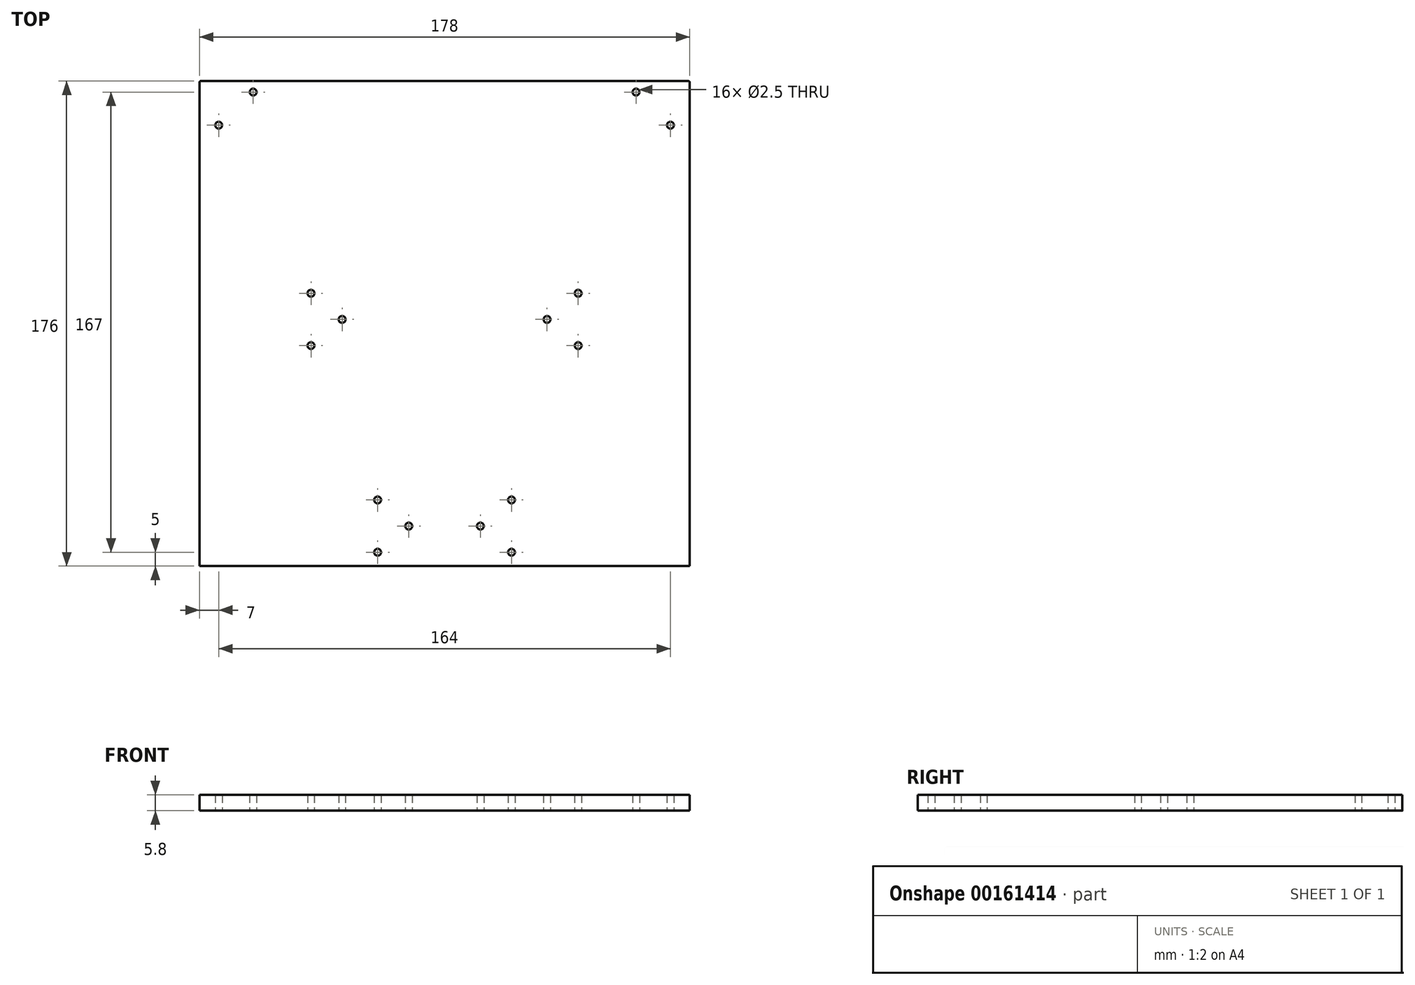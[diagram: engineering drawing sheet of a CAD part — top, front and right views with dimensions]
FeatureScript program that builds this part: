
annotation { "Feature Type Name" : "Feature", "Feature Type Description" : "" }
export const myFeature = defineFeature(function(context is Context, id is Id, definition is map)
    precondition{}
    {
        {
            var Q0;
            Q0=qCreatedBy(makeId("Top.planeOp"),FACE);
            var sketch = newSketch(context, id + "F0", { "sketchPlane" : qUnion([Q0])});
            skLineSegment(sketch, "E0.bottom", {"start": v(88.5, 88) * mm, "end": v(-88.5, 88) * mm});
            skLineSegment(sketch, "E0.top", {"start": v(89, -88) * mm, "end": v(58.5, -88) * mm});
            skLineSegment(sketch, "E0.left", {"start": v(89, 87.5) * mm, "end": v(89, -88) * mm});
            skLineSegment(sketch, "E0.right", {"start": v(-89, 87.5) * mm, "end": v(-89, -88) * mm});
            skPoint(sketch, "E0.middle", {"position": v(0, 0) * mm});
            skLineSegment(sketch, "E1.trimOffspring", {"start": v(2, -88) * mm, "end": v(-89, -88) * mm});
            skLineSegment(sketch, "E2", {"start": v(2, -88) * mm, "end": v(58.5, -88) * mm});
            skPoint(sketch, "E3", {"position": v(-69.5, 84) * mm});
            skPoint(sketch, "E4", {"position": v(-82, 72) * mm});
            skPoint(sketch, "E5", {"position": v(69.5, 84) * mm});
            skPoint(sketch, "E6", {"position": v(82, 72) * mm});
            skCircle(sketch, "E7", {"center": v(-69.5, 84) * mm, "radius": 1.25 * mm});
            skCircle(sketch, "E8", {"center": v(-82, 72) * mm, "radius": 1.25 * mm});
            skCircle(sketch, "E9", {"center": v(82, 72) * mm, "radius": 1.25 * mm});
            skCircle(sketch, "E10", {"center": v(69.5, 84) * mm, "radius": 1.25 * mm});
            skPoint(sketch, "E11", {"position": v(48.5, 11) * mm});
            skPoint(sketch, "E12", {"position": v(37.2, 1.5) * mm});
            skPoint(sketch, "E13", {"position": v(48.5, -8) * mm});
            skPoint(sketch, "E14", {"position": v(-48.5, 11) * mm});
            skPoint(sketch, "E15", {"position": v(-37.2, 1.5) * mm});
            skPoint(sketch, "E16", {"position": v(-48.5, -8) * mm});
            skCircle(sketch, "E17", {"center": v(-48.5, 11) * mm, "radius": 1.25 * mm});
            skCircle(sketch, "E18", {"center": v(-37.2, 1.5) * mm, "radius": 1.25 * mm});
            skCircle(sketch, "E19", {"center": v(-48.5, -8) * mm, "radius": 1.25 * mm});
            skCircle(sketch, "E20", {"center": v(37.2, 1.5) * mm, "radius": 1.25 * mm});
            skCircle(sketch, "E21", {"center": v(48.5, 11) * mm, "radius": 1.25 * mm});
            skCircle(sketch, "E22", {"center": v(48.5, -8) * mm, "radius": 1.25 * mm});
            skPoint(sketch, "E23.visualSharp", {"position": v(89, 88) * mm});
            skArc(sketch, "E23.filletArc", {"start": v(89, 87.5) * mm, "mid": v(88.85, 87.85) * mm, "end": v(88.5, 88) * mm});
            skPoint(sketch, "E24.visualSharp", {"position": v(-89, 88) * mm});
            skArc(sketch, "E24.filletArc", {"start": v(-88.5, 88) * mm, "mid": v(-88.85, 87.85) * mm, "end": v(-89, 87.5) * mm});
            skPoint(sketch, "E25", {"position": v(24.3, -64) * mm});
            skPoint(sketch, "E26", {"position": v(13, -73.5) * mm});
            skPoint(sketch, "E27", {"position": v(24.3, -83) * mm});
            skCircle(sketch, "E28", {"center": v(13, -73.5) * mm, "radius": 1.25 * mm});
            skCircle(sketch, "E29", {"center": v(24.3, -64) * mm, "radius": 1.25 * mm});
            skCircle(sketch, "E30", {"center": v(24.3, -83) * mm, "radius": 1.25 * mm});
            skPoint(sketch, "E31", {"position": v(-24.3, -64) * mm});
            skPoint(sketch, "E32", {"position": v(-13, -73.5) * mm});
            skPoint(sketch, "E33", {"position": v(-24.3, -83) * mm});
            skCircle(sketch, "E34", {"center": v(-24.3, -64) * mm, "radius": 1.25 * mm});
            skCircle(sketch, "E35", {"center": v(-13, -73.5) * mm, "radius": 1.25 * mm});
            skCircle(sketch, "E36", {"center": v(-24.3, -83) * mm, "radius": 1.25 * mm});
            skSolve(sketch);
        }
        {
            var Q0;
            Q0=makeQuery(id+"F0.imprint","IMPRINT",FACE,{"disambiguationData":[TD([[makeQuery(id+"F0.imprint","IMPRINT",EDGE,{"derivedFrom":sQuery(id+"F0.wireOp",EDGE,"E0.bottom")}),1.0]])]});
            extrude(context, id + "F1", {"entities" : qUnion([Q0]), "depth" : 5.8 * mm});
        }
    });
